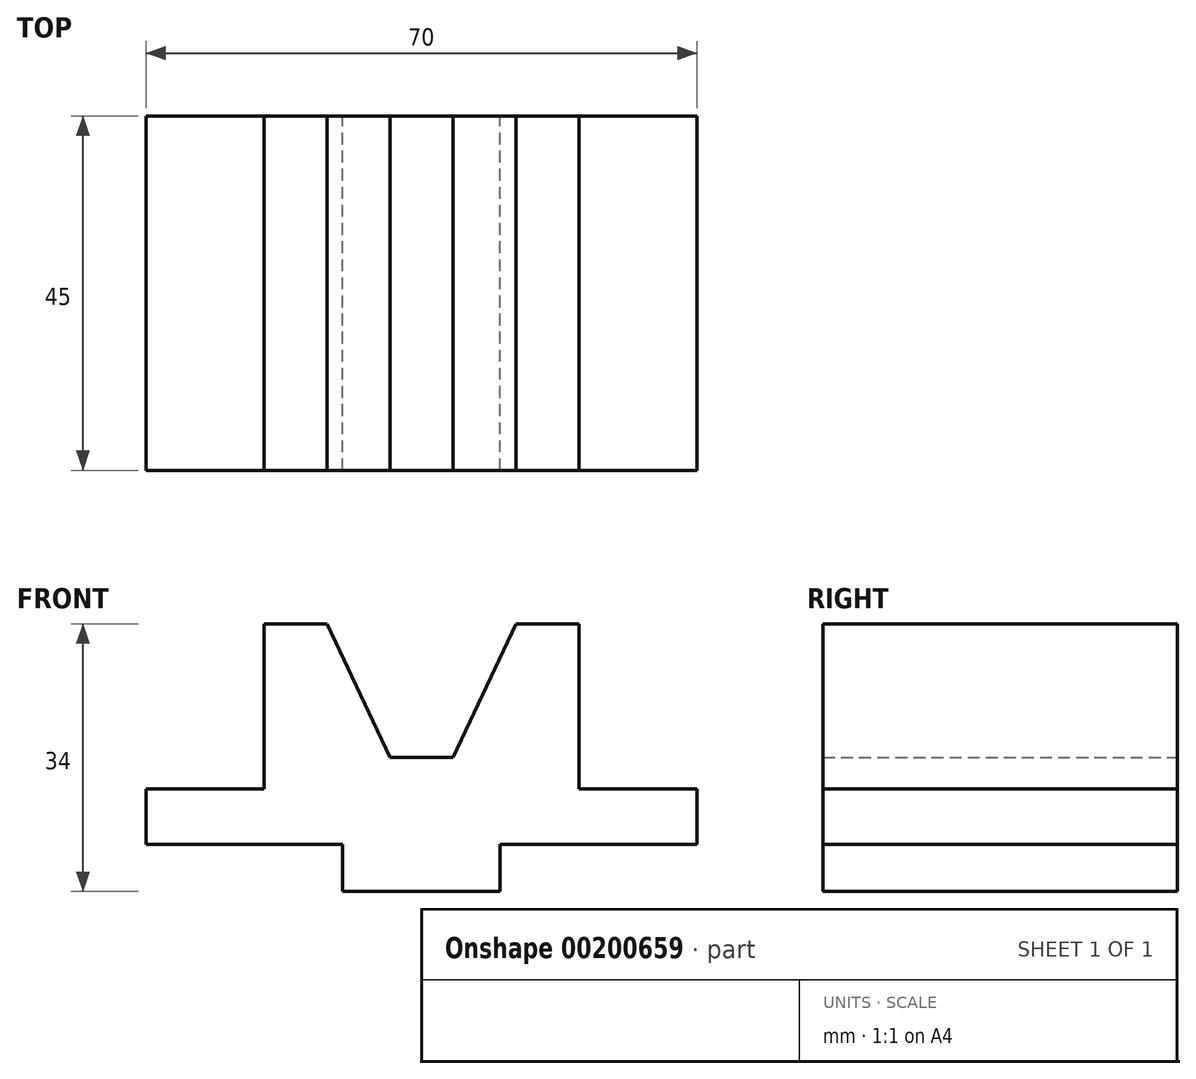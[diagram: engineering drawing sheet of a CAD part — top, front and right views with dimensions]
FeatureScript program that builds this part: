
annotation { "Feature Type Name" : "Feature", "Feature Type Description" : "" }
export const myFeature = defineFeature(function(context is Context, id is Id, definition is map)
    precondition{}
    {
        {
            var Q0;
            Q0=qCreatedBy(makeId("Front.planeOp"),FACE);
            var sketch = newSketch(context, id + "F0", { "sketchPlane" : qUnion([Q0])});
            skLineSegment(sketch, "E0", {"start": v(0, 65.3) * mm, "end": v(0, -64.5) * mm, "construction": true});
            skLineSegment(sketch, "E1", {"start": v(-10, 0) * mm, "end": v(10, 0) * mm});
            skLineSegment(sketch, "E2", {"start": v(10, 0) * mm, "end": v(10, 6) * mm});
            skLineSegment(sketch, "E3", {"start": v(10, 6) * mm, "end": v(35, 6) * mm});
            skLineSegment(sketch, "E4", {"start": v(35, 6) * mm, "end": v(35, 13) * mm});
            skLineSegment(sketch, "E5", {"start": v(35, 13) * mm, "end": v(20, 13) * mm});
            skLineSegment(sketch, "E6", {"start": v(20, 13) * mm, "end": v(20, 34) * mm});
            skLineSegment(sketch, "E7", {"start": v(20, 34) * mm, "end": v(12, 34) * mm});
            skLineSegment(sketch, "E8", {"start": v(-4, 17) * mm, "end": v(4, 17) * mm});
            skLineSegment(sketch, "E9", {"start": v(12, 34) * mm, "end": v(4, 17) * mm});
            skLineSegment(sketch, "E10.MirrorCS", {"start": v(-12, 34) * mm, "end": v(-4, 17) * mm});
            skLineSegment(sketch, "E11.MirrorCS", {"start": v(-20, 34) * mm, "end": v(-12, 34) * mm});
            skLineSegment(sketch, "E12.MirrorCS", {"start": v(-20, 13) * mm, "end": v(-20, 34) * mm});
            skLineSegment(sketch, "E13.MirrorCS", {"start": v(-35, 13) * mm, "end": v(-20, 13) * mm});
            skLineSegment(sketch, "E14.MirrorCS", {"start": v(-35, 6) * mm, "end": v(-35, 13) * mm});
            skLineSegment(sketch, "E15.MirrorCS", {"start": v(-10, 6) * mm, "end": v(-35, 6) * mm});
            skLineSegment(sketch, "E16.MirrorCS", {"start": v(10, 0) * mm, "end": v(-10, 0) * mm});
            skLineSegment(sketch, "E17.MirrorCS", {"start": v(-10, 0) * mm, "end": v(-10, 6) * mm});
            skSolve(sketch);
        }
        {
            var Q0;
            Q0=makeQuery(id+"F0.imprint","IMPRINT",FACE,{"disambiguationData":[TD([[makeQuery(id+"F0.imprint","IMPRINT",EDGE,{"derivedFrom":sQuery(id+"F0.wireOp",EDGE,"E2")}),1.0]])]});
            extrude(context, id + "F1", {"entities" : qUnion([Q0]), "depth" : 45 * mm});
        }
    });
